# Revit family: IS_Connect_Multiproduct_BIM_NL_E8232;E8245
name_source: partatom
category: Plumbing Fixtures
revit_build: Autodesk Revit MEP 2014 (Build: 20130308_1515(x64)
units: mm (PartAtom-declared; Revit-internal decimal feet)

## types (2) — shared parameters
Accessories = www.idealstandardnederland.nl
AreaUnits = millimeters
Assembly Code = C1030200
AssetType = Vast
BREEAMApproved = No
Brand = Ideal Standard
CodePerformance = DIN EN 997 CL1-6AC/5A, DIN EN 33
ConnectionType = Sanitair
Default Elevation = 400 mm  [stored 1.31234 ft]
Description = Connect wandcloset 540 mm van keramiek. DIN EN 997. Diepspoel. Geglazuurde spoelrand. Geschikt voor Spoeling vanaf 4,5 Liter. Exclusief closetzitting.
DurationUnit = jaar
ECA = No
ExpectedLife = 25
Features = Wandcloset 540 mm van keramiek. DIN EN 997. Diepspoel. Geglazuurde spoelrand. Geschikt voor Spoeling vanaf 4,5 Liter. Exclusief closetzitting.
Finish = Wit
IfcExportAs = IfcSanitaryTerminalType
IfcExportType = TOILETPAN
InstallationInstructions = http://www.idealstandardnederland.nl
LinearUnits = millimeters
ManufacturerURL = www.idealstandardnederland.nl
ModelReference = Connect wandcloset 540 mm van keramiek. DIN EN 997. Diepspoel. Geglazuurde spoelrand. Geschikt voor Spoeling vanaf 4,5 Liter. Exclusief closetzitting.
NBSDescription = WC pans
NBSReference = 45-30-70/384
NominalHeight = 337 mm
NominalLength = 540 mm
NominalWidth = 361 mm
PanColor = Wit
PanMaterial = Keramiek
PanMounting = BackToWall
ProductInformation = http://www.idealstandardnederland.nl
Shape = Gesculptuurd
Size = 360 x 540 x 337 mm
Space = Internal
ToiletPanType = WashDown
ToiletType = Other
URL = www.idealstandardnederland.nl
Uniclass2015Code = Pr_40_20_93_94
Uniclass2015Title = WC pans
Uniclass2015Version = Products v1.1
Version = 1
VolumeUnits = liter
WRAS = No
WarrantyDescription = Fabrieksgarantie
WarrantyDurationParts = 5
WarrantyDurationUnit = jaar
WaterEfficientProduct = No
zero-valued in all types: CWFU, Cost, HWFU, NominalDepth, SpilloverLevel, WFU

## per-type parameters (varying)
| type | BIMObjectName | BarCode | Model | ModelNumber | Name | NettWeight |
| E823201 - CONNECT WANDWC WIT | ISI_IdealStandard_WcPans_E823201 | 5017830448754 | E823201 | E823201 | WcPans_E823201_IdealStandard | 22.762 kg |
| E824501 - CONNECT/CONCEPT WANDCLOSET | ISI_IdealStandard_WcPans_E824501 | 5017830488248 | E824501 | E824501 | WcPans_E824501_IdealStandard | 25.06 kg |

note: [stored X ft] marks values corroborated as IEEE doubles in the binary element streams (Revit-internal decimal feet)

## geometry (parser evidence)
native form markers: Sweep x1
no freeform markers — native parametric forms only
